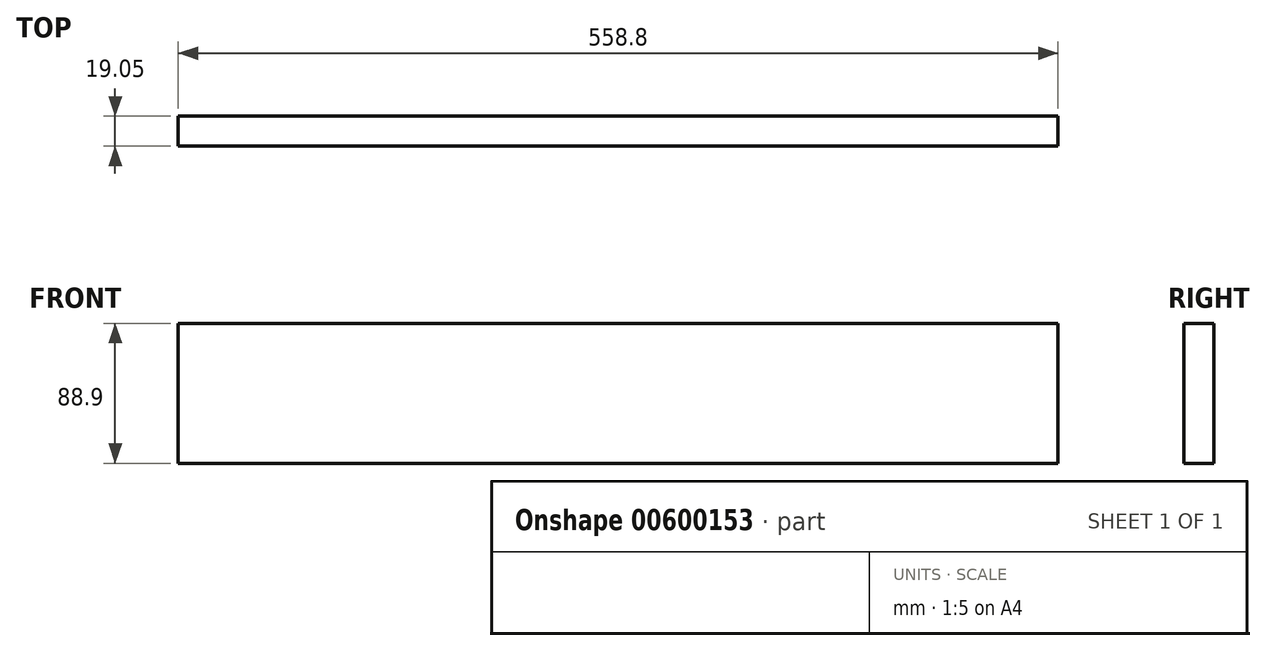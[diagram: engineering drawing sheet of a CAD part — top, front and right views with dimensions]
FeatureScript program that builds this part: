
annotation { "Feature Type Name" : "Feature", "Feature Type Description" : "" }
export const myFeature = defineFeature(function(context is Context, id is Id, definition is map)
    precondition{}
    {
        {
            var Q0;
            Q0=qCreatedBy(makeId("Front.planeOp"),FACE);
            var sketch = newSketch(context, id + "F0", { "sketchPlane" : qUnion([Q0])});
            skLineSegment(sketch, "E0.bottom", {"start": v(-279.4, 44.45) * mm, "end": v(279.4, 44.45) * mm});
            skLineSegment(sketch, "E0.top", {"start": v(-279.4, -44.45) * mm, "end": v(279.4, -44.45) * mm});
            skLineSegment(sketch, "E0.left", {"start": v(-279.4, 44.45) * mm, "end": v(-279.4, -44.45) * mm});
            skLineSegment(sketch, "E0.right", {"start": v(279.4, 44.45) * mm, "end": v(279.4, -44.45) * mm});
            skLineSegment(sketch, "E1", {"start": v(-279.4, -44.45) * mm, "end": v(279.4, 44.45) * mm, "construction": true});
            skSolve(sketch);
        }
        {
            var Q0;
            Q0 = qSketchRegion(id + "F0", true);
            extrude(context, id + "F1", {"entities" : qUnion([Q0]), "depth" : 19.05 * mm, "offsetDistance" : 25.4 * mm});
        }
    });
